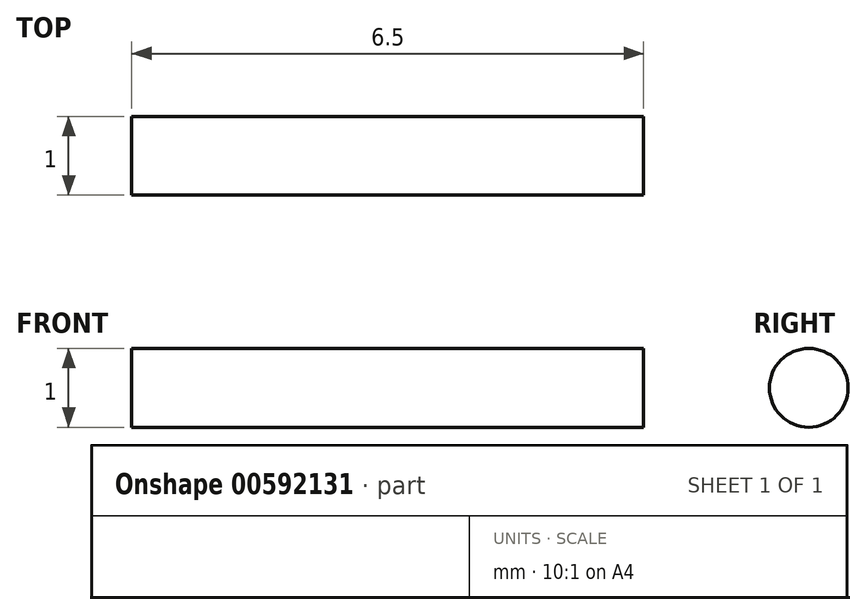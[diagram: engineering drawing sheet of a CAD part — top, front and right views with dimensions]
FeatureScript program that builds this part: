
annotation { "Feature Type Name" : "Feature", "Feature Type Description" : "" }
export const myFeature = defineFeature(function(context is Context, id is Id, definition is map)
    precondition{}
    {
        {
            var Q0;
            Q0=qCreatedBy(makeId("Front.planeOp"),FACE);
            var sketch = newSketch(context, id + "F0", { "sketchPlane" : qUnion([Q0])});
            skLineSegment(sketch, "E0", {"start": v(-6.5, 0) * mm, "end": v(6.5, 0) * mm});
            skLineSegment(sketch, "E1", {"start": v(-6.5, 0) * mm, "end": v(-6.5, 1) * mm});
            skLineSegment(sketch, "E2", {"start": v(6.5, 0) * mm, "end": v(6.5, 1) * mm});
            skLineSegment(sketch, "E3", {"start": v(6.5, 1) * mm, "end": v(-6.5, 1) * mm});
            skSolve(sketch);
        }
        {
            var Q0;
            Q0 = qSketchRegion(id + "F0", true);
            var Q1;
            Q1=sQuery(id+"F0.wireOp",EDGE,"E0");
            revolve(context, id + "F1", {"entities" : qUnion([Q0]), "axis" : qUnion([Q1]), "revolveType" : RevolveType.FULL});
        }
        {
            var Q0;
            Q0=makeQuery(id+"F1.opRevolve","SWEPT_BODY",BODY,{"disambiguationData":[OSD([sQuery(id+"F0.wireOp",EDGE,"E0"),sQuery(id+"F0.wireOp",EDGE,"E1"),sQuery(id+"F0.wireOp",EDGE,"E2"),sQuery(id+"F0.wireOp",EDGE,"E3")])]});
            var Q1;
            Q1=qCreatedBy(makeId("Origin.pointOp"),VERTEX);
            transform(context, id + "F2", {"entities" : qUnion([Q0]), "transformType" : TransformType.SCALE_UNIFORMLY, "scale" : .5, "scalePoint" : qUnion([Q1]), "makeCopy" : false});
        }
    });
